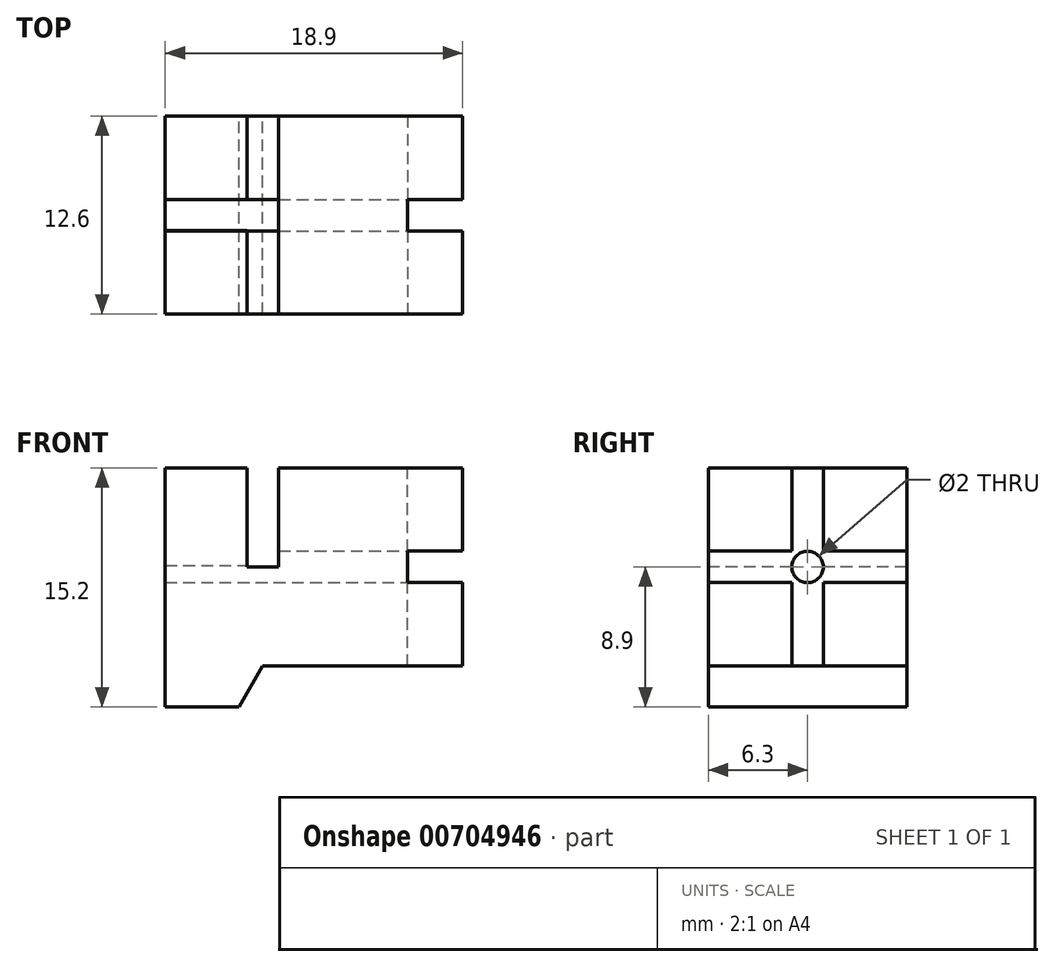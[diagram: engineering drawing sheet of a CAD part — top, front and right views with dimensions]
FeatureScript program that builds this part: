
annotation { "Feature Type Name" : "Feature", "Feature Type Description" : "" }
export const myFeature = defineFeature(function(context is Context, id is Id, definition is map)
    precondition{}
    {
        {
            var Q0;
            Q0=qCreatedBy(makeId("Front.planeOp"),FACE);
            var sketch = newSketch(context, id + "F0", { "sketchPlane" : qUnion([Q0])});
            skLineSegment(sketch, "E0.bottom", {"start": v(0, 0) * mm, "end": v(18.9, 0) * mm});
            skLineSegment(sketch, "E0.left", {"start": v(0, 0) * mm, "end": v(0, -12.6) * mm});
            skLineSegment(sketch, "E0.right", {"start": v(18.9, 0) * mm, "end": v(18.9, -12.6) * mm});
            skLineSegment(sketch, "E1", {"start": v(0, -12.6) * mm, "end": v(0, -15.2) * mm});
            skLineSegment(sketch, "E2", {"start": v(0, -15.2) * mm, "end": v(4.7, -15.2) * mm});
            skLineSegment(sketch, "E3", {"start": v(4.7, -15.2) * mm, "end": v(6.2, -12.6) * mm});
            skLineSegment(sketch, "E4", {"start": v(18.9, -12.6) * mm, "end": v(6.2, -12.6) * mm});
            skLineSegment(sketch, "E5", {"start": v(0, -12.6) * mm, "end": v(6.2, -12.6) * mm, "construction": true});
            skSolve(sketch);
        }
        {
            var Q0;
            Q0 = qSketchRegion(id + "F0", true);
            extrude(context, id + "F1", {"entities" : qUnion([Q0]), "depth" : 12.6 * mm, "offsetDistance" : 25 * mm});
        }
        {
            var Q0;
            Q0=makeQuery(id+"F1.opExtrude","CAP_FACE",FACE,{"disambiguationData":[OSD([sQuery(id+"F0.wireOp",EDGE,"E0.bottom"),sQuery(id+"F0.wireOp",EDGE,"E0.left"),sQuery(id+"F0.wireOp",EDGE,"E0.right"),sQuery(id+"F0.wireOp",EDGE,"E1"),sQuery(id+"F0.wireOp",EDGE,"E2"),sQuery(id+"F0.wireOp",EDGE,"E3"),sQuery(id+"F0.wireOp",EDGE,"E4")])],"isStart":false});
            var sketch = newSketch(context, id + "F2", { "sketchPlane" : qUnion([Q0])});
            skLineSegment(sketch, "E6", {"start": v(5.2, 0) * mm, "end": v(5.2, -6.3) * mm});
            skLineSegment(sketch, "E7", {"start": v(5.2, -6.3) * mm, "end": v(7.2, -6.3) * mm});
            skLineSegment(sketch, "E8", {"start": v(7.2, -6.3) * mm, "end": v(7.2, 0) * mm});
            skSolve(sketch);
        }
        {
            var Q0;
            {var subQ0=sQuery(id+"F2.wireOp",EDGE,"E6");Q0=makeQuery(id+"F2.imprint","IMPRINT",FACE,{"disambiguationData":[TD([[makeQuery(id+"F2.imprint","IMPRINT",EDGE,{"derivedFrom":subQ0}),1.0]])]});}
            extrude(context, id + "F3", {"entities" : qUnion([Q0]), "operationType" : NewBodyOperationType.REMOVE, "endBound" : BoundingType.THROUGH_ALL, "oppositeDirection" : true, "depth" : 25 * mm, "offsetDistance" : 25 * mm});
        }
        {
            var Q0;
            Q0=makeQuery(id+"F1.opExtrude","SWEPT_FACE",FACE,{"disambiguationData":[OSD([sQuery(id+"F0.wireOp",EDGE,"E0.left"),sQuery(id+"F0.wireOp",EDGE,"E1")])]});
            var sketch = newSketch(context, id + "F4", { "sketchPlane" : qUnion([Q0])});
            skPoint(sketch, "E9", {"position": v(6.3, 0) * mm});
            skLineSegment(sketch, "E10", {"start": v(6.3, 0) * mm, "end": v(6.3, -6.2) * mm, "construction": true});
            skLineSegment(sketch, "E11", {"start": v(7.3, -6.2) * mm, "end": v(7.3, 0) * mm});
            skLineSegment(sketch, "E12.MirrorCS", {"start": v(5.3, -6.2) * mm, "end": v(5.3, 0) * mm});
            skLineSegment(sketch, "E13", {"start": v(7.3, -6.2) * mm, "end": v(5.3, -6.2) * mm});
            skSolve(sketch);
        }
        {
            var Q0;
            {var subQ0=sQuery(id+"F4.wireOp",EDGE,"E11");Q0=makeQuery(id+"F4.imprint","IMPRINT",FACE,{"disambiguationData":[TD([[makeQuery(id+"F4.imprint","IMPRINT",EDGE,{"derivedFrom":subQ0}),1.0]])]});}
            extrude(context, id + "F5", {"entities" : qUnion([Q0]), "operationType" : NewBodyOperationType.REMOVE, "oppositeDirection" : true, "depth" : 7.2 * mm, "offsetDistance" : 25 * mm});
        }
        {
            var Q0;
            Q0=makeQuery(id+"F1.opExtrude","CAP_FACE",FACE,{"disambiguationData":[OSD([sQuery(id+"F0.wireOp",EDGE,"E0.bottom"),sQuery(id+"F0.wireOp",EDGE,"E0.left"),sQuery(id+"F0.wireOp",EDGE,"E0.right"),sQuery(id+"F0.wireOp",EDGE,"E1"),sQuery(id+"F0.wireOp",EDGE,"E2"),sQuery(id+"F0.wireOp",EDGE,"E3"),sQuery(id+"F0.wireOp",EDGE,"E4")])],"isStart":false});
            var sketch = newSketch(context, id + "F6", { "sketchPlane" : qUnion([Q0])});
            skLineSegment(sketch, "E14.bottom", {"start": v(18.9, -5.3) * mm, "end": v(15.4, -5.3) * mm});
            skLineSegment(sketch, "E14.top", {"start": v(18.9, -7.3) * mm, "end": v(15.4, -7.3) * mm});
            skLineSegment(sketch, "E14.left", {"start": v(18.9, -5.3) * mm, "end": v(18.9, -7.3) * mm});
            skLineSegment(sketch, "E14.right", {"start": v(15.4, -5.3) * mm, "end": v(15.4, -7.3) * mm});
            skPoint(sketch, "E14.middle", {"position": v(17.15, -6.3) * mm});
            skPoint(sketch, "E14.middle.positionSnap0", {"position": v(18.9, -6.3) * mm});
            skPoint(sketch, "E14.centerSnap0", {"position": v(18.9, -6.3) * mm});
            skSolve(sketch);
        }
        {
            var Q0;
            Q0=makeQuery(id+"F6.imprint","IMPRINT",FACE,{"disambiguationData":[TD([[makeQuery(id+"F6.imprint","IMPRINT",EDGE,{"derivedFrom":sQuery(id+"F6.wireOp",EDGE,"E14.bottom")}),1.0]])]});
            extrude(context, id + "F7", {"entities" : qUnion([Q0]), "operationType" : NewBodyOperationType.REMOVE, "endBound" : BoundingType.THROUGH_ALL, "oppositeDirection" : true, "depth" : 25 * mm, "offsetDistance" : 25 * mm});
        }
        {
            var Q0;
            {var subQ4=sQuery(id+"F0.wireOp",EDGE,"E0.right");var subQ6=sQuery(id+"F0.wireOp",EDGE,"E0.bottom");Q0=makeQuery(id+"F3.boolean.opBoolean","SPLIT",FACE,{"disambiguationData":[TD([makeQuery(id+"F1.opExtrude","SWEPT_FACE",FACE,{"disambiguationData":[OSD([subQ4])]})])],"derivedFrom":makeQuery(id+"F1.opExtrude","SWEPT_FACE",FACE,{"disambiguationData":[OSD([subQ6])]})});}
            var sketch = newSketch(context, id + "F8", { "sketchPlane" : qUnion([Q0])});
            skLineSegment(sketch, "E15.bottom", {"start": v(18.9, -5.3) * mm, "end": v(15.4, -5.3) * mm});
            skLineSegment(sketch, "E15.top", {"start": v(18.9, -7.3) * mm, "end": v(15.4, -7.3) * mm});
            skLineSegment(sketch, "E15.left", {"start": v(18.9, -5.3) * mm, "end": v(18.9, -7.3) * mm});
            skLineSegment(sketch, "E15.right", {"start": v(15.4, -5.3) * mm, "end": v(15.4, -7.3) * mm});
            skPoint(sketch, "E15.middle", {"position": v(17.15, -6.3) * mm});
            skPoint(sketch, "E15.middle.positionSnap0", {"position": v(18.9, -6.3) * mm});
            skPoint(sketch, "E15.centerSnap0", {"position": v(18.9, -6.3) * mm});
            skSolve(sketch);
        }
        {
            var Q0;
            Q0=makeQuery(id+"F8.imprint","IMPRINT",FACE,{"disambiguationData":[TD([[makeQuery(id+"F8.imprint","IMPRINT",EDGE,{"derivedFrom":sQuery(id+"F8.wireOp",EDGE,"E15.bottom")}),1.0]])]});
            extrude(context, id + "F9", {"entities" : qUnion([Q0]), "operationType" : NewBodyOperationType.REMOVE, "endBound" : BoundingType.THROUGH_ALL, "oppositeDirection" : true, "depth" : 25 * mm, "offsetDistance" : 25 * mm});
        }
        {
            var Q0;
            Q0=makeQuery(id+"F9.boolean.opBoolean","MERGE",FACE,{"derivedFrom":[makeQuery(id+"F7.boolean.opBoolean","COPY",FACE,{"derivedFrom":makeQuery(id+"F7.opExtrude","SWEPT_FACE",FACE,{"disambiguationData":[OSD([sQuery(id+"F6.wireOp",EDGE,"E14.right")])]})}),makeQuery(id+"F9.opExtrude","SWEPT_FACE",FACE,{"disambiguationData":[OSD([sQuery(id+"F8.wireOp",EDGE,"E15.right")])]})]});
            var sketch = newSketch(context, id + "F10", { "sketchPlane" : qUnion([Q0])});
            skCircle(sketch, "E16", {"center": v(-6.3, -6.3) * mm, "radius": 1.41 * mm, "construction": true});
            skPoint(sketch, "E16.first.point", {"position": v(-7.3, -5.3) * mm});
            skPoint(sketch, "E16.second.point", {"position": v(-5.3, -5.3) * mm});
            skPoint(sketch, "E16.third.point", {"position": v(-5.3, -7.3) * mm});
            skCircle(sketch, "E17", {"center": v(-6.3, -6.3) * mm, "radius": 1 * mm});
            skSolve(sketch);
        }
        {
            var Q0;
            Q0=makeQuery(id+"F10.imprint","IMPRINT",FACE,{"disambiguationData":[TD([[makeQuery(id+"F10.imprint","IMPRINT",EDGE,{"derivedFrom":sQuery(id+"F10.wireOp",EDGE,"E17")}),1.0]])]});
            extrude(context, id + "F11", {"entities" : qUnion([Q0]), "operationType" : NewBodyOperationType.REMOVE, "endBound" : BoundingType.THROUGH_ALL, "oppositeDirection" : true, "depth" : 25 * mm, "offsetDistance" : 25 * mm});
        }
    });
